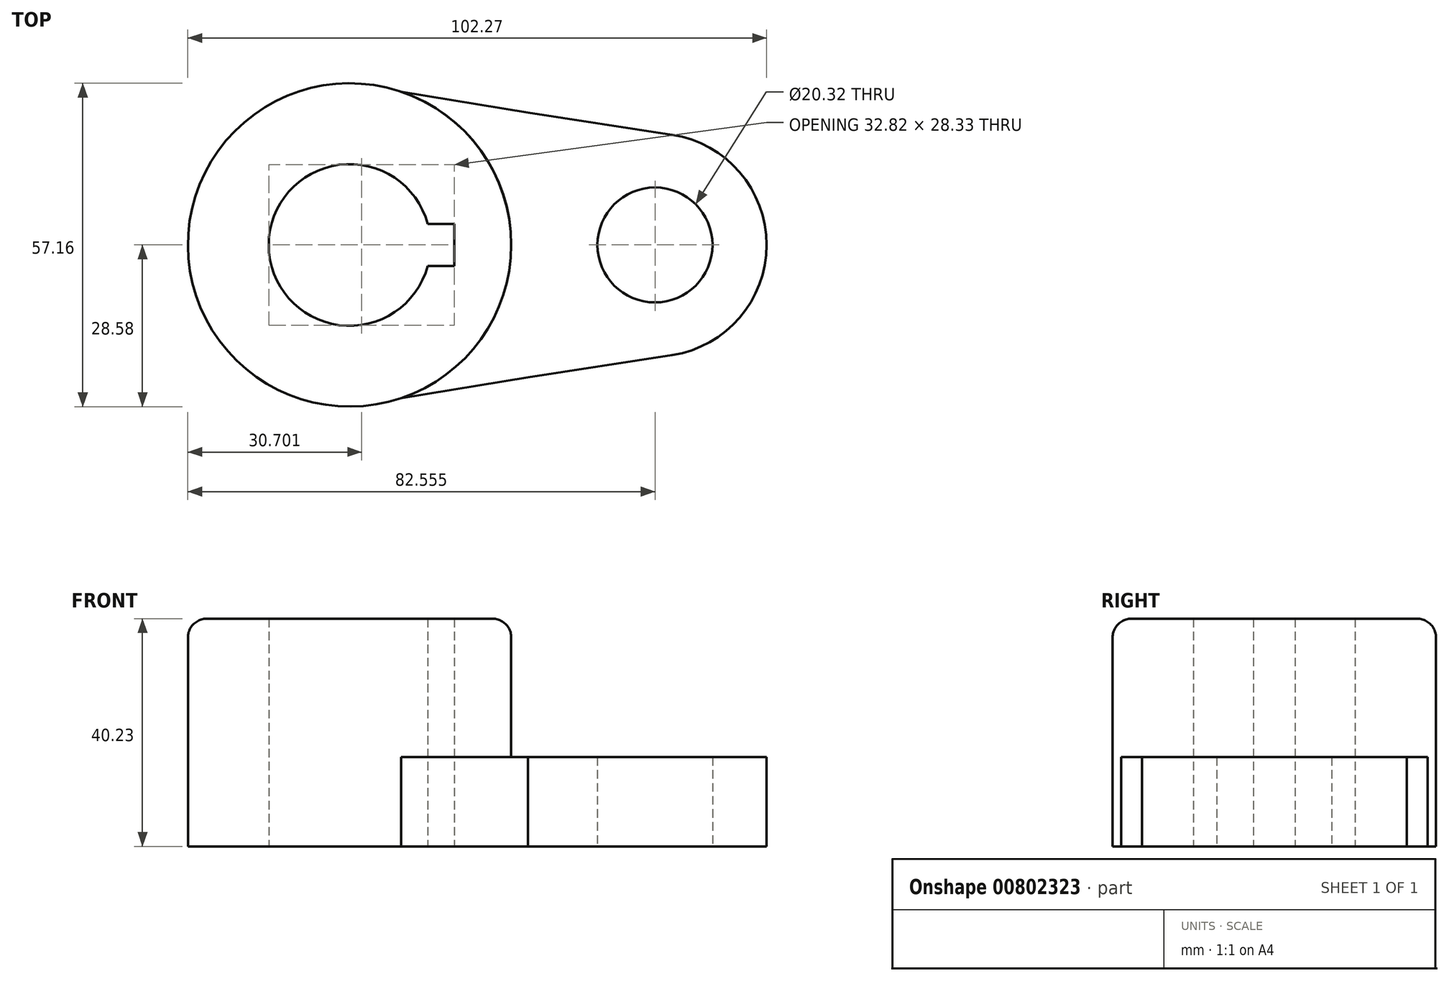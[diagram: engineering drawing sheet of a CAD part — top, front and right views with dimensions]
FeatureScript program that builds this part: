
annotation { "Feature Type Name" : "Feature", "Feature Type Description" : "" }
export const myFeature = defineFeature(function(context is Context, id is Id, definition is map)
    precondition{}
    {
        {
            var Q0;
            Q0=qCreatedBy(makeId("Top.planeOp"),FACE);
            var sketch = newSketch(context, id + "F0", { "sketchPlane" : qUnion([Q0])});
            skArc(sketch, "E0", {"start": v(13.8, 3.7) * mm, "mid": v(-14.29, 0) * mm, "end": v(13.8, -3.7) * mm});
            skCircle(sketch, "E1", {"center": v(0, 0) * mm, "radius": 28.58 * mm});
            skCircle(sketch, "E2", {"center": v(53.98, 0) * mm, "radius": 10.16 * mm});
            skLineSegment(sketch, "E3.right", {"start": v(18.53, 3.7) * mm, "end": v(18.53, -3.7) * mm});
            skLineSegment(sketch, "E4.bottom", {"start": v(18.53, -3.7) * mm, "end": v(13.8, -3.7) * mm});
            skLineSegment(sketch, "E4.top", {"start": v(18.53, 3.7) * mm, "end": v(13.8, 3.7) * mm});
            skLineSegment(sketch, "E4.left", {"start": v(18.53, -3.7) * mm, "end": v(18.53, 3.7) * mm});
            skPoint(sketch, "E5.orphan", {"position": v(-18.53, -3.7) * mm});
            skPoint(sketch, "E6.orphan", {"position": v(-18.53, 3.7) * mm});
            skPoint(sketch, "E7.orphan", {"position": v(-14.29, 13.63) * mm});
            skPoint(sketch, "E8.orphan", {"position": v(-14.29, 6.81) * mm});
            skPoint(sketch, "E3.left.end.orphan", {"position": v(-14.29, 0) * mm});
            skArc(sketch, "E9", {"start": v(56.97, -19.49) * mm, "mid": v(73.69, 0) * mm, "end": v(56.97, 19.49) * mm});
            skPoint(sketch, "E10.end.orphan", {"position": v(53.98, 19.71) * mm});
            skPoint(sketch, "E11.start.orphan", {"position": v(53.98, -19.71) * mm});
            skLineSegment(sketch, "E12", {"start": v(9.14, 27.08) * mm, "end": v(31.56, 23.4) * mm});
            skLineSegment(sketch, "E13", {"start": v(9.14, -27.08) * mm, "end": v(31.56, -23.4) * mm});
            skLineSegment(sketch, "E14", {"start": v(31.56, 23.4) * mm, "end": v(56.97, 19.49) * mm});
            skLineSegment(sketch, "E15", {"start": v(56.97, -19.49) * mm, "end": v(31.56, -23.4) * mm});
            skSolve(sketch);
        }
        {
            var Q0;
            Q0=makeQuery(id+"F0.imprint","IMPRINT",FACE,{"disambiguationData":[TD([[makeQuery(id+"F0.imprint","IMPRINT",EDGE,{"derivedFrom":sQuery(id+"F0.wireOp",EDGE,"E0")}),-1.0]])]});
            extrude(context, id + "F1", {"entities" : qUnion([Q0]), "depth" : 40.23 * mm, "offsetDistance" : 25.4 * mm});
        }
        {
            var Q0;
            Q0=makeQuery(id+"F0.imprint","IMPRINT",FACE,{"disambiguationData":[TD([[makeQuery(id+"F0.imprint","IMPRINT",EDGE,{"derivedFrom":sQuery(id+"F0.wireOp",EDGE,"E2")}),-1.0]])]});
            extrude(context, id + "F2", {"entities" : qUnion([Q0]), "operationType" : NewBodyOperationType.ADD, "depth" : 15.77 * mm, "offsetDistance" : 25.4 * mm});
        }
        {
            var Q0;
            Q0=makeQuery(id+"F1.opExtrude","CAP_EDGE",EDGE,{"disambiguationData":[OSD([sQuery(id+"F0.wireOp",EDGE,"E1")])],"isStart":false});
            fillet(context, id + "F3", {"entities" : qUnion([Q0]), "radius" : 3.3 * mm, "tangentPropagation" : true, "allowEdgeOverflow" : false});
        }
    });
